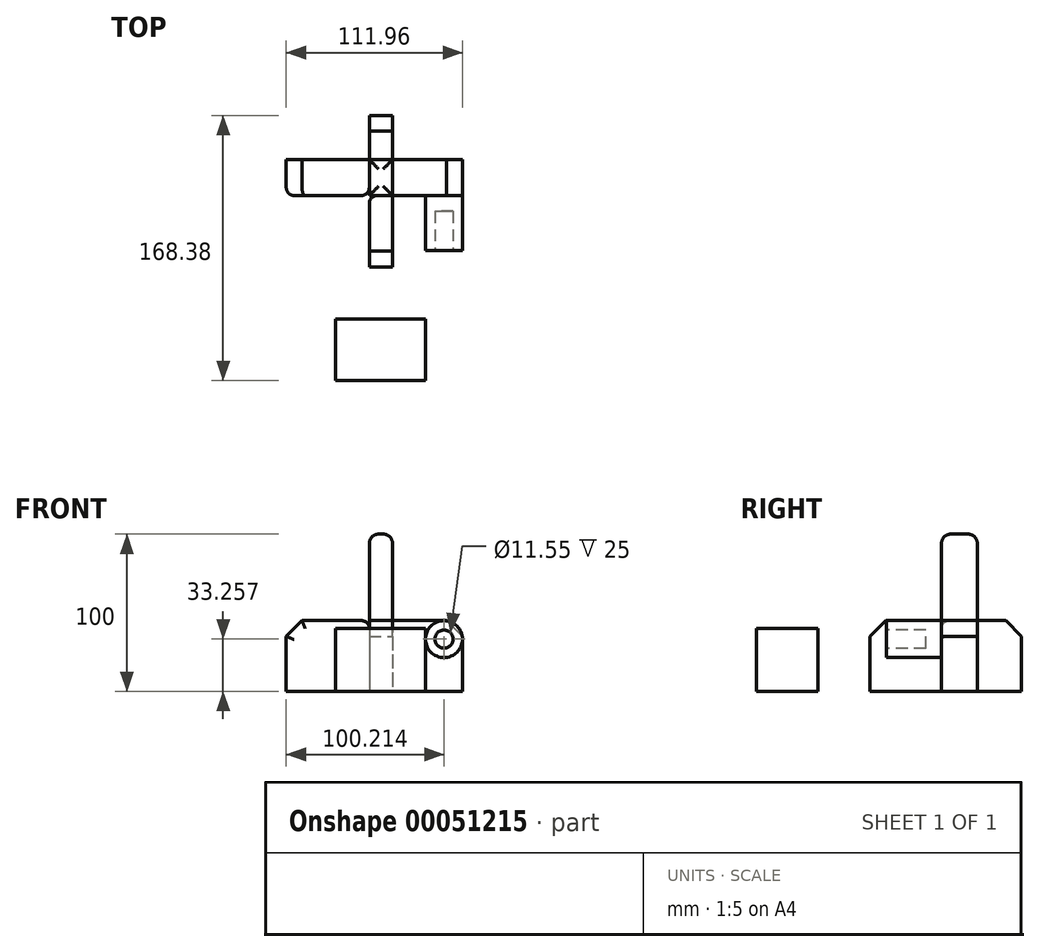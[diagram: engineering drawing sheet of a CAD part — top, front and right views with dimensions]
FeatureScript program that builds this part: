
annotation { "Feature Type Name" : "Feature", "Feature Type Description" : "" }
export const myFeature = defineFeature(function(context is Context, id is Id, definition is map)
    precondition{}
    {
        {
            var Q0;
            Q0=qCreatedBy(makeId("Top.planeOp"),FACE);
            var sketch = newSketch(context, id + "F0", { "sketchPlane" : qUnion([Q0])});
            skLineSegment(sketch, "E0.bottom", {"start": v(14.77, 50.84) * mm, "end": v(0, 50.84) * mm});
            skLineSegment(sketch, "E0.top", {"start": v(14.77, -45.35) * mm, "end": v(0, -45.35) * mm});
            skLineSegment(sketch, "E0.left", {"start": v(14.77, 50.84) * mm, "end": v(14.77, -45.35) * mm});
            skLineSegment(sketch, "E0.right", {"start": v(0, 50.84) * mm, "end": v(0, -45.35) * mm});
            skLineSegment(sketch, "E1.bottom", {"start": v(-52.76, 0) * mm, "end": v(59.2, 0) * mm});
            skLineSegment(sketch, "E1.top", {"start": v(-52.76, 22.7) * mm, "end": v(59.2, 22.7) * mm});
            skLineSegment(sketch, "E1.left", {"start": v(-52.76, 0) * mm, "end": v(-52.76, 22.7) * mm});
            skLineSegment(sketch, "E1.right", {"start": v(59.2, 0) * mm, "end": v(59.2, 22.7) * mm});
            skSolve(sketch);
        }
        {
            var Q0;
            {var subQ5=sQuery(id+"F0.wireOp",EDGE,"E1.left");Q0=makeQuery(id+"F0.imprint","IMPRINT",FACE,{"disambiguationData":[TD([[makeQuery(id+"F0.imprint","IMPRINT",EDGE,{"derivedFrom":subQ5}),-1.0]])]});}
            var Q1;
            {var subQ0=sQuery(id+"F0.wireOp",EDGE,"E0.top");Q1=makeQuery(id+"F0.imprint","IMPRINT",FACE,{"disambiguationData":[TD([[makeQuery(id+"F0.imprint","IMPRINT",EDGE,{"derivedFrom":subQ0}),-1.0]])]});}
            var Q2;
            {var subQ5=sQuery(id+"F0.wireOp",EDGE,"E1.right");Q2=makeQuery(id+"F0.imprint","IMPRINT",FACE,{"disambiguationData":[TD([[makeQuery(id+"F0.imprint","IMPRINT",EDGE,{"derivedFrom":subQ5}),1.0]])]});}
            var Q3;
            {var subQ0=sQuery(id+"F0.wireOp",EDGE,"E0.bottom");Q3=makeQuery(id+"F0.imprint","IMPRINT",FACE,{"disambiguationData":[TD([[makeQuery(id+"F0.imprint","IMPRINT",EDGE,{"derivedFrom":subQ0}),1.0]])]});}
            extrude(context, id + "F10", {"entities" : qUnion([Q0, Q1, Q2, Q3]), "depth" : 45 * mm});
        }
        {
            var Q0;
            {var subQ0=sQuery(id+"F0.wireOp",EDGE,"E1.bottom");Q0=makeQuery(id+"F10.opExtrude","SWEPT_FACE",FACE,{"disambiguationData":[OSD([subQ0]),TDD([makeQuery(id+"F0.imprint","IMPRINT",EDGE,{"disambiguationData":[TD([[makeQuery(id+"F0.imprint","INTERSECT",VERTEX,{"derivedFrom":[subQ0,sQuery(id+"F0.wireOp",EDGE,"E1.right")]}),1.0]])],"derivedFrom":subQ0})])]});}
            var sketch = newSketch(context, id + "F1", { "sketchPlane" : qUnion([Q0])});
            skCircle(sketch, "E2", {"center": v(47.45, 33.26) * mm, "radius": 11.74 * mm});
            skSolve(sketch);
        }
        {
            var Q0;
            {var subQ0=sQuery(id+"F1.wireOp",EDGE,"E2");var subQ1=sQuery(id+"F0.wireOp",EDGE,"E1.right");var subQ2=sQuery(id+"F0.wireOp",EDGE,"E1.bottom");var subQ3=makeQuery(id+"F1.imprint","INTERSECT",VERTEX,{"derivedFrom":[makeQuery(id+"F10.opExtrude","SWEPT_EDGE",EDGE,{"disambiguationData":[OSD([subQ2,subQ1])]}),subQ0]});Q0=makeQuery(id+"F1.imprint","IMPRINT",FACE,{"disambiguationData":[TD([[makeQuery(id+"F1.imprint","IMPRINT",EDGE,{"disambiguationData":[TD([[subQ3,-1.0]])],"derivedFrom":subQ0}),1.0]])]});}
            extrude(context, id + "F2", {"entities" : qUnion([Q0]), "depth" : 35 * mm});
        }
        {
            var Q0;
            Q0=makeQuery(id+"F10.opExtrude","CAP_EDGE",EDGE,{"disambiguationData":[OSD([sQuery(id+"F0.wireOp",EDGE,"E0.top")])],"isStart":false});
            var Q1;
            Q1=makeQuery(id+"F10.opExtrude","CAP_EDGE",EDGE,{"disambiguationData":[OSD([sQuery(id+"F0.wireOp",EDGE,"E0.bottom")])],"isStart":false});
            var Q2;
            Q2=makeQuery(id+"F10.opExtrude","CAP_EDGE",EDGE,{"disambiguationData":[OSD([sQuery(id+"F0.wireOp",EDGE,"E1.right")])],"isStart":false});
            var Q3;
            Q3=makeQuery(id+"F10.opExtrude","CAP_EDGE",EDGE,{"disambiguationData":[OSD([sQuery(id+"F0.wireOp",EDGE,"E1.left")])],"isStart":false});
            chamfer(context, id + "F3", {"entities" : qUnion([Q0, Q1, Q2, Q3]), "width" : 10 * mm, "tangentPropagation" : true});
        }
        {
            var Q0;
            {var subQ0=sQuery(id+"F0.wireOp",EDGE,"E1.top");var subQ1=sQuery(id+"F0.wireOp",EDGE,"E0.left");var subQ2=makeQuery(id+"F0.imprint","INTERSECT",VERTEX,{"derivedFrom":[subQ1,subQ0]});Q0=makeQuery(id+"F0.imprint","IMPRINT",FACE,{"disambiguationData":[TD([[makeQuery(id+"F0.imprint","IMPRINT",EDGE,{"disambiguationData":[TD([[subQ2,-1.0]])],"derivedFrom":subQ1}),-1.0]])]});}
            var sketch = newSketch(context, id + "F4", { "sketchPlane" : qUnion([Q0])});
            skSolve(sketch);
        }
        {
            var Q0;
            Q0 = qSketchRegion(id + "F4", true);
            var Q1;
            {var subQ0=sQuery(id+"F0.wireOp",EDGE,"E1.top");var subQ1=sQuery(id+"F0.wireOp",EDGE,"E0.left");var subQ2=makeQuery(id+"F0.imprint","INTERSECT",VERTEX,{"derivedFrom":[subQ1,subQ0]});Q1=makeQuery(id+"F4.imprint","IMPRINT",FACE,{"disambiguationData":[TD([[makeQuery(id+"F4.imprint","IMPRINT",EDGE,{"derivedFrom":makeQuery(id+"F0.imprint","IMPRINT",EDGE,{"disambiguationData":[TD([[subQ2,-1.0]])],"derivedFrom":subQ1})}),-1.0]])]});}
            extrude(context, id + "F5", {"entities" : qUnion([Q0, Q1]), "depth" : 100 * mm});
        }
        {
            var Q0;
            Q0=makeQuery(id+"F5.opExtrude","CAP_FACE",FACE,{"disambiguationData":[OSD([sQuery(id+"F0.wireOp",EDGE,"E0.left"),sQuery(id+"F0.wireOp",EDGE,"E0.right"),sQuery(id+"F0.wireOp",EDGE,"E1.bottom"),sQuery(id+"F0.wireOp",EDGE,"E1.top")])],"isStart":false});
            fillet(context, id + "F11", {"entities" : qUnion([Q0]), "radius" : 6 * mm, "tangentPropagation" : true, "allowEdgeOverflow" : false});
        }
        {
            var Q0;
            Q0=makeQuery(id+"F2.opExtrude","CAP_FACE",FACE,{"disambiguationData":[OSD([sQuery(id+"F1.wireOp",EDGE,"E2")])],"isStart":false});
            var sketch = newSketch(context, id + "F6", { "sketchPlane" : qUnion([Q0])});
            skCircle(sketch, "E3", {"center": v(47.45, 33.26) * mm, "radius": 5.78 * mm});
            skSolve(sketch);
        }
        {
            var Q0;
            Q0 = qSketchRegion(id + "F6", true);
            extrude(context, id + "F7", {"entities" : qUnion([Q0]), "operationType" : NewBodyOperationType.REMOVE, "oppositeDirection" : true, "depth" : 25 * mm});
        }
        {
            var Q0;
            {var subQ0=sQuery(id+"F0.wireOp",EDGE,"E1.bottom");var subQ1=sQuery(id+"F0.wireOp",EDGE,"E0.right");Q0=makeQuery(id+"F10.opExtrude","SWEPT_EDGE",EDGE,{"disambiguationData":[OSD([subQ1,subQ0]),ownerDisambiguation([makeQuery(id+"F10.opExtrude","SWEPT_BODY",BODY,{"disambiguationData":[OSD([sQuery(id+"F0.wireOp",EDGE,"E0.top"),sQuery(id+"F0.wireOp",EDGE,"E0.left"),subQ1,subQ0])]})])]});}
            fillet(context, id + "F12", {"entities" : qUnion([Q0]), "radius" : 5 * mm, "tangentPropagation" : true, "allowEdgeOverflow" : false});
        }
        {
            var Q0;
            {var subQ0=sQuery(id+"F0.wireOp",EDGE,"E1.left");var subQ1=sQuery(id+"F0.wireOp",EDGE,"E1.bottom");Q0=makeQuery(id+"F3.opChamfer","BLEND_EDGE",EDGE,{"blendedFrom":[makeQuery(id+"F10.opExtrude","CAP_EDGE",EDGE,{"disambiguationData":[OSD([subQ0])],"isStart":false}),makeQuery(id+"F10.opExtrude","SWEPT_FACE",FACE,{"disambiguationData":[OSD([subQ1]),TDD([makeQuery(id+"F0.imprint","IMPRINT",EDGE,{"disambiguationData":[TD([[makeQuery(id+"F0.imprint","INTERSECT",VERTEX,{"derivedFrom":[subQ1,subQ0]}),-1.0]])],"derivedFrom":subQ1})])]})],"blendedInto":[makeQuery(id+"F10.opExtrude","SWEPT_FACE",FACE,{"disambiguationData":[OSD([subQ1]),TDD([makeQuery(id+"F0.imprint","IMPRINT",EDGE,{"disambiguationData":[TD([[makeQuery(id+"F0.imprint","INTERSECT",VERTEX,{"derivedFrom":[subQ1,subQ0]}),-1.0]])],"derivedFrom":subQ1})])]})]});}
            var Q1;
            {var subQ0=sQuery(id+"F0.wireOp",EDGE,"E1.bottom");Q1=makeQuery(id+"F10.opExtrude","CAP_EDGE",EDGE,{"disambiguationData":[OSD([subQ0]),TDD([makeQuery(id+"F0.imprint","IMPRINT",EDGE,{"disambiguationData":[TD([[makeQuery(id+"F0.imprint","INTERSECT",VERTEX,{"derivedFrom":[subQ0,sQuery(id+"F0.wireOp",EDGE,"E1.left")]}),-1.0]])],"derivedFrom":subQ0})])],"isStart":false});}
            var Q2;
            Q2=makeQuery(id+"F10.opExtrude","SWEPT_EDGE",EDGE,{"disambiguationData":[OSD([sQuery(id+"F0.wireOp",EDGE,"E1.bottom"),sQuery(id+"F0.wireOp",EDGE,"E1.left")])]});
            fillet(context, id + "F13", {"entities" : qUnion([Q0, Q1, Q2]), "radius" : 5 * mm, "tangentPropagation" : true, "allowEdgeOverflow" : false});
        }
        {
            var Q0;
            Q0=qCreatedBy(makeId("Top.planeOp"),FACE);
            var sketch = newSketch(context, id + "F8", { "sketchPlane" : qUnion([Q0])});
            skLineSegment(sketch, "E4.bottom", {"start": v(35.58, -78.36) * mm, "end": v(-21.33, -78.36) * mm});
            skLineSegment(sketch, "E4.top", {"start": v(35.58, -117.54) * mm, "end": v(-21.33, -117.54) * mm});
            skLineSegment(sketch, "E4.left", {"start": v(35.58, -78.36) * mm, "end": v(35.58, -117.54) * mm});
            skLineSegment(sketch, "E4.right", {"start": v(-21.33, -78.36) * mm, "end": v(-21.33, -117.54) * mm});
            skSolve(sketch);
        }
        {
            var Q0;
            Q0 = qSketchRegion(id + "F8", true);
            extrude(context, id + "F9", {"entities" : qUnion([Q0]), "depth" : 40 * mm});
        }
    });
